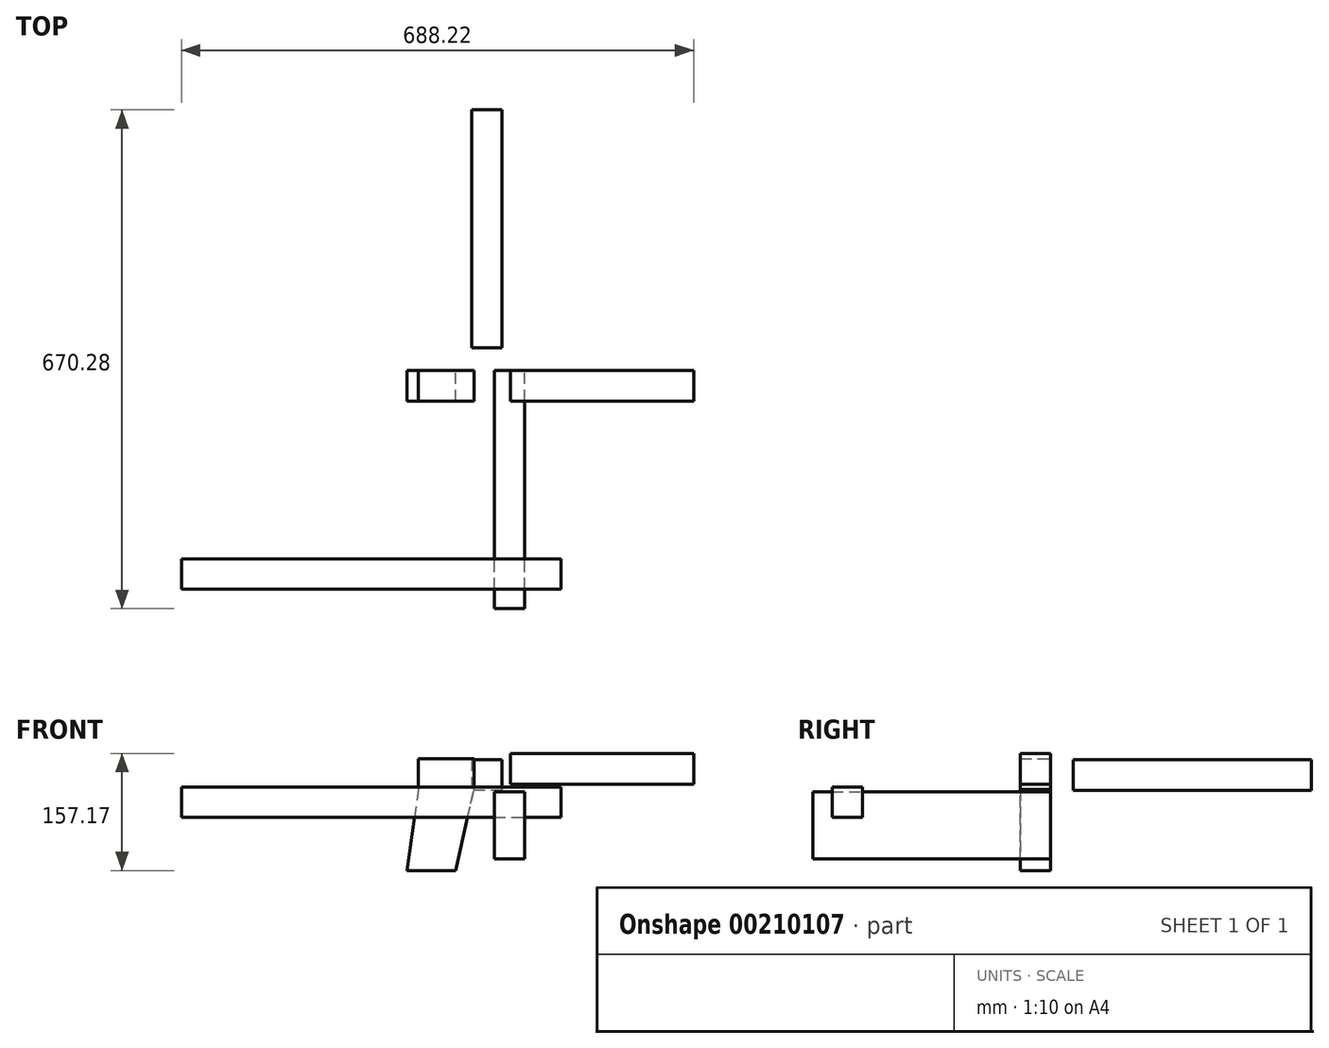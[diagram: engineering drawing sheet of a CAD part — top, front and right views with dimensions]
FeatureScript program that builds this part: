
annotation { "Feature Type Name" : "Feature", "Feature Type Description" : "" }
export const myFeature = defineFeature(function(context is Context, id is Id, definition is map)
    precondition{}
    {
        {
            var Q0;
            Q0=qCreatedBy(makeId("Front.planeOp"),FACE);
            var sketch = newSketch(context, id + "F0", { "sketchPlane" : qUnion([Q0])});
            skLineSegment(sketch, "E0", {"start": v(-71.59, 78.64) * mm, "end": v(-71.59, 37.64) * mm});
            skLineSegment(sketch, "E1", {"start": v(-71.59, 37.64) * mm, "end": v(-86.59, -71.36) * mm});
            skLineSegment(sketch, "E2", {"start": v(-86.59, -71.36) * mm, "end": v(-21.65, -71.36) * mm});
            skLineSegment(sketch, "E3", {"start": v(-21.65, -71.36) * mm, "end": v(3.41, 37.64) * mm});
            skLineSegment(sketch, "E4", {"start": v(3.41, 37.64) * mm, "end": v(3.41, 78.64) * mm});
            skLineSegment(sketch, "E5", {"start": v(3.41, 78.64) * mm, "end": v(-71.59, 78.64) * mm});
            skSolve(sketch);
        }
        {
            var Q0;
            Q0=qSketchRegion(id+"F0",true);
            extrude(context, id + "F1", {"entities" : qUnion([Q0]), "depth" : 41 * mm});
        }
        {
            var Q0;
            Q0=qCreatedBy(makeId("Front.planeOp"),FACE);
            var sketch = newSketch(context, id + "F2", { "sketchPlane" : qUnion([Q0])});
            skLineSegment(sketch, "E6", {"start": v(52.4, 85.81) * mm, "end": v(52.4, 44.81) * mm});
            skLineSegment(sketch, "E7", {"start": v(52.4, 44.81) * mm, "end": v(298.4, 44.81) * mm});
            skLineSegment(sketch, "E8", {"start": v(298.4, 44.81) * mm, "end": v(298.4, 85.81) * mm});
            skLineSegment(sketch, "E9", {"start": v(298.4, 85.81) * mm, "end": v(52.4, 85.81) * mm});
            skSolve(sketch);
        }
        {
            var Q0;
            Q0=qSketchRegion(id+"F2",true);
            extrude(context, id + "F3", {"entities" : qUnion([Q0]), "depth" : 41 * mm});
        }
        {
            var Q0;
            Q0=qCreatedBy(makeId("Right.planeOp"),FACE);
            var sketch = newSketch(context, id + "F4", { "sketchPlane" : qUnion([Q0])});
            skLineSegment(sketch, "E10", {"start": v(30.28, 77.41) * mm, "end": v(30.28, 36.41) * mm});
            skLineSegment(sketch, "E11", {"start": v(30.28, 36.41) * mm, "end": v(350.28, 36.41) * mm});
            skLineSegment(sketch, "E12", {"start": v(350.28, 36.41) * mm, "end": v(350.28, 77.41) * mm});
            skLineSegment(sketch, "E13", {"start": v(350.28, 77.41) * mm, "end": v(30.28, 77.41) * mm});
            skSolve(sketch);
        }
        {
            var Q0;
            Q0=qSketchRegion(id+"F4",true);
            extrude(context, id + "F5", {"entities" : qUnion([Q0]), "depth" : 41 * mm});
        }
        {
            var Q0;
            Q0=qCreatedBy(makeId("Top.planeOp"),FACE);
            var sketch = newSketch(context, id + "F6", { "sketchPlane" : qUnion([Q0])});
            skLineSegment(sketch, "E14", {"start": v(-389.82, -253.01) * mm, "end": v(-389.82, -294.01) * mm});
            skLineSegment(sketch, "E15", {"start": v(-389.82, -294.01) * mm, "end": v(120.18, -294.01) * mm});
            skLineSegment(sketch, "E16", {"start": v(120.18, -294.01) * mm, "end": v(120.18, -253.01) * mm});
            skLineSegment(sketch, "E17", {"start": v(120.18, -253.01) * mm, "end": v(-389.82, -253.01) * mm});
            skSolve(sketch);
        }
        {
            var Q0;
            Q0=makeQuery(id+"F6.imprint","IMPRINT",FACE,{"disambiguationData":[TD([[makeQuery(id+"F6.imprint","IMPRINT",EDGE,{"derivedFrom":sQuery(id+"F6.wireOp",EDGE,"E14")}),1.0]])]});
            extrude(context, id + "F7", {"entities" : qUnion([Q0]), "depth" : 41 * mm});
        }
        {
            var Q0;
            Q0=qCreatedBy(makeId("Front.planeOp"),FACE);
            var sketch = newSketch(context, id + "F8", { "sketchPlane" : qUnion([Q0])});
            skLineSegment(sketch, "E18", {"start": v(71.46, 34.43) * mm, "end": v(30.46, 34.43) * mm});
            skLineSegment(sketch, "E19", {"start": v(30.46, 34.43) * mm, "end": v(30.46, -55.57) * mm});
            skLineSegment(sketch, "E20", {"start": v(30.46, -55.57) * mm, "end": v(71.46, -55.57) * mm});
            skLineSegment(sketch, "E21", {"start": v(71.46, -55.57) * mm, "end": v(71.46, 34.43) * mm});
            skSolve(sketch);
        }
        {
            var Q0;
            Q0=makeQuery(id+"F8.imprint","IMPRINT",FACE,{"disambiguationData":[TD([[makeQuery(id+"F8.imprint","IMPRINT",EDGE,{"derivedFrom":sQuery(id+"F8.wireOp",EDGE,"E18")}),1.0]])]});
            extrude(context, id + "F9", {"entities" : qUnion([Q0]), "depth" : 320 * mm});
        }
    });
